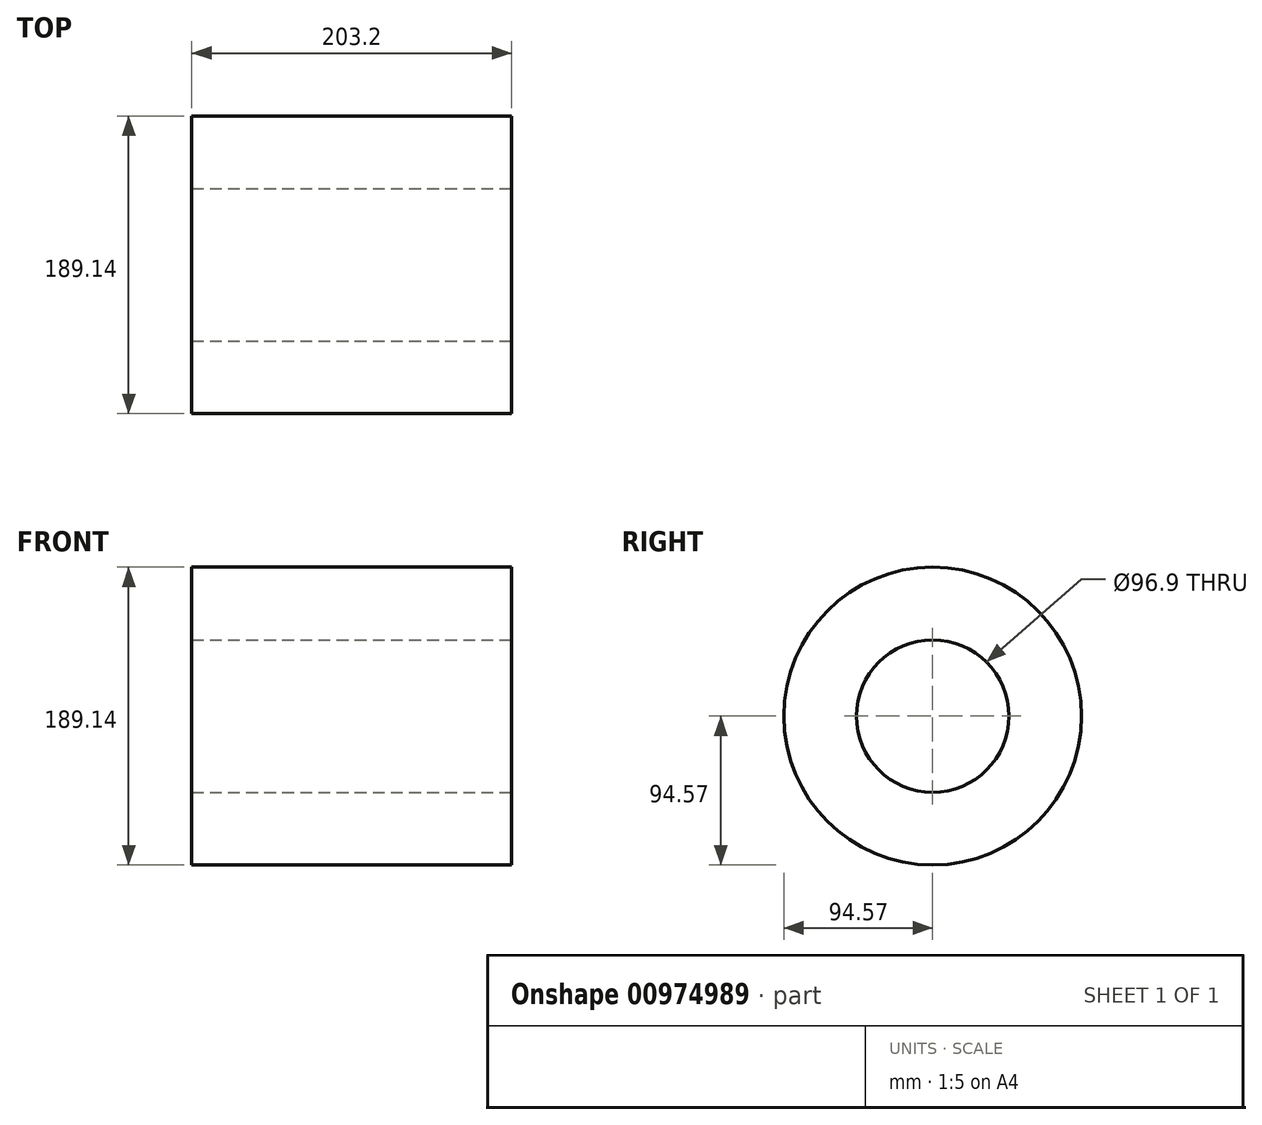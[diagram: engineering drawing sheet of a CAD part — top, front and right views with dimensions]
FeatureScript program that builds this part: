
annotation { "Feature Type Name" : "Feature", "Feature Type Description" : "" }
export const myFeature = defineFeature(function(context is Context, id is Id, definition is map)
    precondition{}
    {
        {
            var Q0;
            Q0=qCreatedBy(makeId("Front.planeOp"),FACE);
            var sketch = newSketch(context, id + "F0", { "sketchPlane" : qUnion([Q0])});
            skLineSegment(sketch, "E0", {"start": v(0, 48.45) * mm, "end": v(0, 94.57) * mm});
            skLineSegment(sketch, "E1", {"start": v(-203.2, 48.45) * mm, "end": v(-203.2, 94.57) * mm});
            skLineSegment(sketch, "E2", {"start": v(0, 94.57) * mm, "end": v(-203.2, 94.57) * mm});
            skLineSegment(sketch, "E3", {"start": v(0, 48.45) * mm, "end": v(-203.2, 48.45) * mm});
            skPoint(sketch, "E4.orphan", {"position": v(-203.2, 0) * mm});
            skPoint(sketch, "E5.orphan", {"position": v(0, 0) * mm});
            skSolve(sketch);
        }
        {
            var Q0;
            Q0=qCreatedBy(makeId("Front.planeOp"),FACE);
            var sketch = newSketch(context, id + "F1", { "sketchPlane" : qUnion([Q0])});
            skLineSegment(sketch, "E6", {"start": v(0, 0) * mm, "end": v(-213.93, 0) * mm});
            skSolve(sketch);
        }
        {
            var Q0;
            Q0=makeQuery(id+"F0.imprint","IMPRINT",FACE,{"disambiguationData":[TD([[makeQuery(id+"F0.imprint","IMPRINT",EDGE,{"derivedFrom":sQuery(id+"F0.wireOp",EDGE,"E0")}),1.0]])]});
            var Q1;
            Q1=sQuery(id+"F1.wireOp",EDGE,"E6");
            revolve(context, id + "F2", {"surfaceOperationType" : NewSurfaceOperationType.NEW, "entities" : qUnion([Q0]), "axis" : qUnion([Q1]), "revolveType" : RevolveType.FULL});
        }
    });
